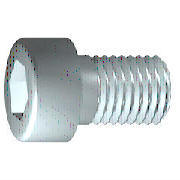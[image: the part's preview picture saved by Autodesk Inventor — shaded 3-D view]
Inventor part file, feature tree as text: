
AUTODESK INVENTOR PART (.ipt)
format: ipt  version: 2020 (Build 240168000, 168)  size: 192,512 bytes
history: native  units: mm (DEFAULTED — no unit token found)
features: sketch x2, other x1, extrude x1, plane x1, fillet x1
ambient origin geometry x7: Origin, YZ Plane, XY Plane, X Axis, Y Axis, Z Axis, Center Point
bodies: Solid1 (feature_tree)
feature tree (6):
  other  "Bryła"
  extrude  "Szczelina"  Depth=27.0mm
  plane  "Work Plane1"
  fillet  "Fillet2"  Radius=0.61355mm
  sketch  "Szkic1"
  sketch  "Szkic2"
